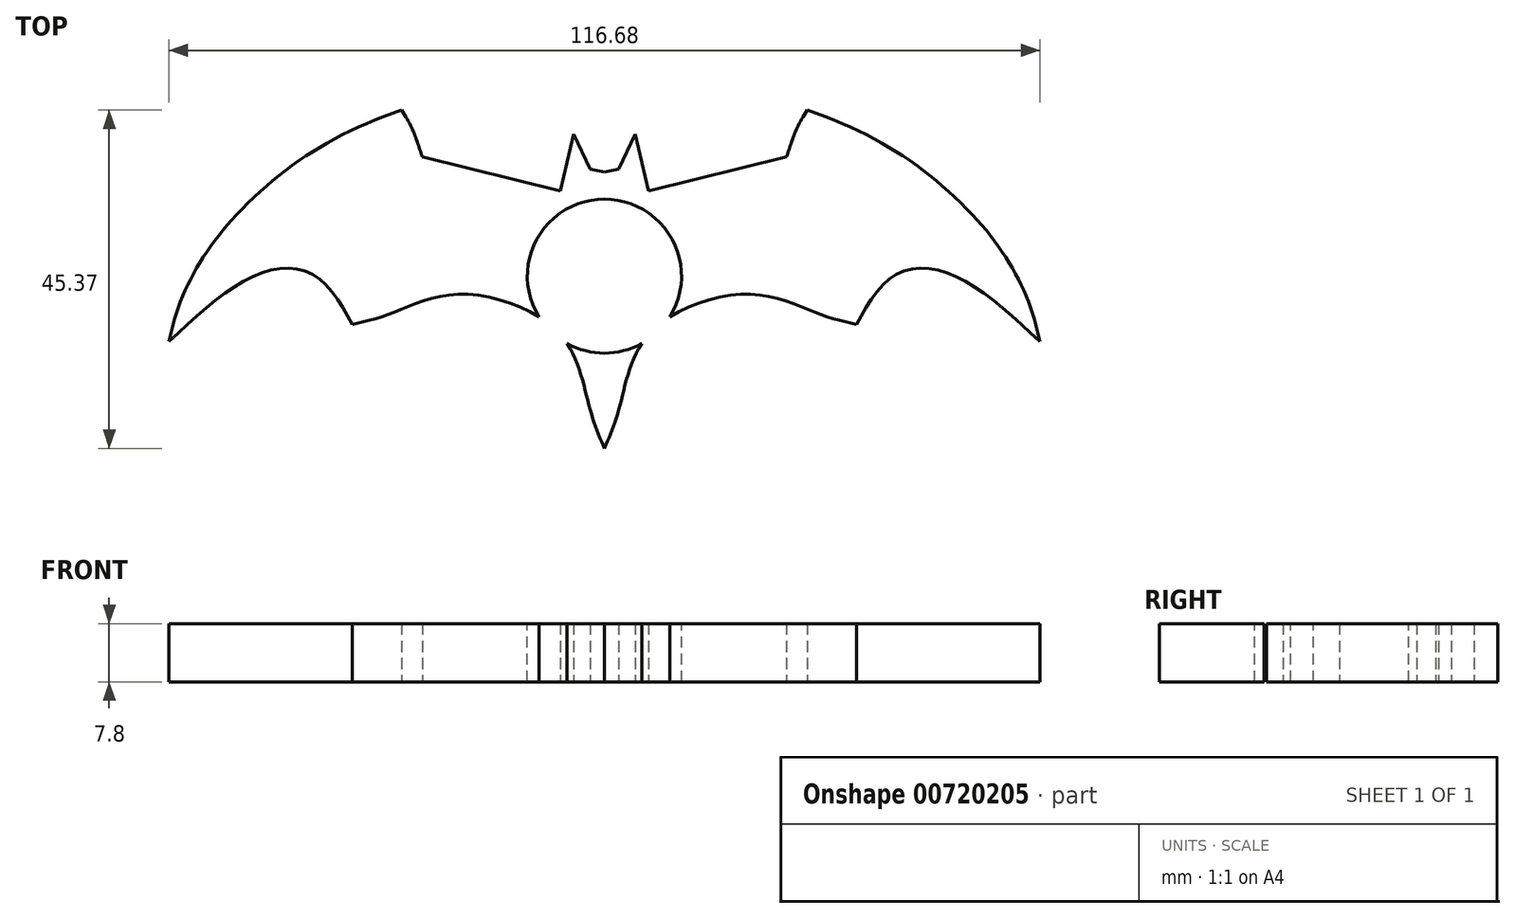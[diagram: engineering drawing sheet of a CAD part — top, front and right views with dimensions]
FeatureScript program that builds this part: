
annotation { "Feature Type Name" : "Feature", "Feature Type Description" : "" }
export const myFeature = defineFeature(function(context is Context, id is Id, definition is map)
    precondition{}
    {
        {
            var Q0;
            Q0=qCreatedBy(makeId("Top.planeOp"),FACE);
            var sketch = newSketch(context, id + "F0", { "sketchPlane" : qUnion([Q0])});
            skFitSpline(sketch, "E0", {"points": [v(28.16, 9) * mm, v(32.71, 14.67) * mm, v(39.1, 14.43) * mm, v(48.61, 7.12) * mm], "startDerivative": vector(11.17, 22.42) * mm, "endDerivative": vector(23.62, -22.06) * mm});
            skFitSpline(sketch, "E1", {"points": [v(48.61, 7.12) * mm, v(41.08, 21.26) * mm], "startDerivative": vector(-2.78, 14.6) * mm, "endDerivative": vector(-12.52, 13.21) * mm});
            skFitSpline(sketch, "E2", {"points": [v(41.08, 21.26) * mm, v(22.65, 32.96) * mm], "startDerivative": vector(-14.9, 15.72) * mm, "endDerivative": vector(-23.64, 8) * mm});
            skFitSpline(sketch, "E3", {"points": [v(22.65, 32.96) * mm, v(20.34, 27.75) * mm], "startDerivative": vector(-4.17, -5.91) * mm, "endDerivative": vector(-1.74, -4.87) * mm});
            skFitSpline(sketch, "E4", {"points": [v(20.34, 27.75) * mm, v(4.92, 23.93) * mm], "startDerivative": vector(-15.41, -3.82) * mm, "endDerivative": vector(-15.41, -3.82) * mm});
            skFitSpline(sketch, "E5", {"points": [v(4.92, 23.93) * mm, v(3.42, 30.3) * mm], "startDerivative": vector(-1.5, 6.37) * mm, "endDerivative": vector(-1.5, 6.37) * mm});
            skFitSpline(sketch, "E6", {"points": [v(3.42, 30.3) * mm, v(1.56, 26.36) * mm], "startDerivative": vector(-1.85, -3.94) * mm, "endDerivative": vector(-1.85, -3.94) * mm});
            skFitSpline(sketch, "E7", {"points": [v(1.56, 26.36) * mm, v(0, 26.05) * mm], "startDerivative": vector(-1.56, -0.3) * mm, "endDerivative": vector(-1.56, -0.3) * mm});
            skFitSpline(sketch, "E8.MirrorCS", {"points": [v(-20.34, 27.75) * mm, v(-4.92, 23.93) * mm], "startDerivative": vector(15.41, -3.82) * mm, "endDerivative": vector(15.41, -3.82) * mm});
            skFitSpline(sketch, "E9.MirrorCS", {"points": [v(-41.08, 21.26) * mm, v(-22.65, 32.96) * mm], "startDerivative": vector(14.9, 15.72) * mm, "endDerivative": vector(23.64, 8) * mm});
            skFitSpline(sketch, "E10.MirrorCS", {"points": [v(-28.16, 9) * mm, v(-32.71, 14.67) * mm, v(-39.1, 14.43) * mm, v(-48.61, 7.12) * mm], "startDerivative": vector(-11.17, 22.42) * mm, "endDerivative": vector(-23.62, -22.06) * mm});
            skFitSpline(sketch, "E11.0", {"points": [v(0, -4.84) * mm, v(1.72, -0.1) * mm, v(5, 7.94) * mm, v(16.3, 12.38) * mm, v(23.87, 10.22) * mm, v(28.16, 9) * mm]});
            skFitSpline(sketch, "E12.MirrorCS", {"points": [v(-48.61, 7.12) * mm, v(-41.08, 21.26) * mm], "startDerivative": vector(2.78, 14.6) * mm, "endDerivative": vector(12.52, 13.21) * mm});
            skFitSpline(sketch, "E13.MirrorCS", {"points": [v(0, -4.84) * mm, v(-1.72, -0.1) * mm, v(-5, 7.94) * mm, v(-16.3, 12.38) * mm, v(-23.87, 10.22) * mm, v(-28.16, 9) * mm]});
            skFitSpline(sketch, "E14.MirrorCS", {"points": [v(-4.92, 23.93) * mm, v(-3.42, 30.3) * mm], "startDerivative": vector(1.5, 6.37) * mm, "endDerivative": vector(1.5, 6.37) * mm});
            skFitSpline(sketch, "E15.MirrorCS", {"points": [v(-3.42, 30.3) * mm, v(-1.56, 26.36) * mm], "startDerivative": vector(1.85, -3.94) * mm, "endDerivative": vector(1.85, -3.94) * mm});
            skFitSpline(sketch, "E16.MirrorCS", {"points": [v(-1.56, 26.36) * mm, v(0, 26.05) * mm], "startDerivative": vector(1.56, -0.3) * mm, "endDerivative": vector(1.56, -0.3) * mm});
            skFitSpline(sketch, "E17.MirrorCS", {"points": [v(-22.65, 32.96) * mm, v(-20.34, 27.75) * mm], "startDerivative": vector(4.17, -5.91) * mm, "endDerivative": vector(1.74, -4.87) * mm});
            skFitSpline(sketch, "E18.MirrorCS", {"points": [v(-3.42, 30.3) * mm, v(-1.56, 26.36) * mm], "startDerivative": vector(1.85, -3.94) * mm, "endDerivative": vector(1.85, -3.94) * mm});
            skSolve(sketch);
        }
        {
            var Q0;
            Q0=makeQuery(id+"F0.imprint","IMPRINT",FACE,{"disambiguationData":[TD([[makeQuery(id+"F0.imprint","IMPRINT",EDGE,{"derivedFrom":sQuery(id+"F0.wireOp",EDGE,"E0")}),1.0]])]});
            extrude(context, id + "F1", {"entities" : qUnion([Q0]), "depth" : 6.5 * mm, "offsetDistance" : 25 * mm});
        }
        {
            var Q0;
            Q0=makeQuery(id+"F1.opExtrude","CAP_FACE",FACE,{"disambiguationData":[OSD([sQuery(id+"F0.wireOp",EDGE,"E0"),sQuery(id+"F0.wireOp",EDGE,"E1"),sQuery(id+"F0.wireOp",EDGE,"E2"),sQuery(id+"F0.wireOp",EDGE,"E3"),sQuery(id+"F0.wireOp",EDGE,"E4"),sQuery(id+"F0.wireOp",EDGE,"E5"),sQuery(id+"F0.wireOp",EDGE,"E6"),sQuery(id+"F0.wireOp",EDGE,"E7"),sQuery(id+"F0.wireOp",EDGE,"E8.MirrorCS"),sQuery(id+"F0.wireOp",EDGE,"E9.MirrorCS"),sQuery(id+"F0.wireOp",EDGE,"E10.MirrorCS"),sQuery(id+"F0.wireOp",EDGE,"E11.0"),sQuery(id+"F0.wireOp",EDGE,"E12.MirrorCS"),sQuery(id+"F0.wireOp",EDGE,"E13.MirrorCS"),sQuery(id+"F0.wireOp",EDGE,"E16.MirrorCS"),sQuery(id+"F0.wireOp",EDGE,"E17.MirrorCS"),sQuery(id+"F0.wireOp",EDGE,"E18.MirrorCS"),sQuery(id+"F0.wireOp",EDGE,"E14.MirrorCS")])],"isStart":false});
            var sketch = newSketch(context, id + "F2", { "sketchPlane" : qUnion([Q0])});
            skCircle(sketch, "E19", {"center": v(-25.83, 20.28) * mm, "radius": 6.01 * mm});
            skCircle(sketch, "E20", {"center": v(0, 14.56) * mm, "radius": 6.33 * mm});
            skCircle(sketch, "E21.MirrorC", {"center": v(25.83, 20.28) * mm, "radius": 6.01 * mm});
            skSolve(sketch);
        }
        {
            var Q0;
            Q0=makeQuery(id+"F1.opExtrude","SWEPT_BODY",BODY,{"disambiguationData":[OSD([sQuery(id+"F0.wireOp",EDGE,"E0"),sQuery(id+"F0.wireOp",EDGE,"E1"),sQuery(id+"F0.wireOp",EDGE,"E2"),sQuery(id+"F0.wireOp",EDGE,"E3"),sQuery(id+"F0.wireOp",EDGE,"E4"),sQuery(id+"F0.wireOp",EDGE,"E5"),sQuery(id+"F0.wireOp",EDGE,"E6"),sQuery(id+"F0.wireOp",EDGE,"E7"),sQuery(id+"F0.wireOp",EDGE,"E8.MirrorCS"),sQuery(id+"F0.wireOp",EDGE,"E9.MirrorCS"),sQuery(id+"F0.wireOp",EDGE,"E10.MirrorCS"),sQuery(id+"F0.wireOp",EDGE,"E11.0"),sQuery(id+"F0.wireOp",EDGE,"E12.MirrorCS"),sQuery(id+"F0.wireOp",EDGE,"E13.MirrorCS"),sQuery(id+"F0.wireOp",EDGE,"E16.MirrorCS"),sQuery(id+"F0.wireOp",EDGE,"E17.MirrorCS"),sQuery(id+"F0.wireOp",EDGE,"E18.MirrorCS"),sQuery(id+"F0.wireOp",EDGE,"E14.MirrorCS")])]});
            var Q1;
            Q1=sQuery(id+"F2.wireOp",VERTEX,"E20.center");
            transform(context, id + "F3", {"entities" : qUnion([Q0]), "transformType" : TransformType.SCALE_UNIFORMLY, "scale" : 1.2, "scalePoint" : qUnion([Q1]), "makeCopy" : false});
        }
        {
            var Q0;
            Q0=makeQuery(id+"F1.opExtrude","CAP_FACE",FACE,{"disambiguationData":[OSD([sQuery(id+"F0.wireOp",EDGE,"E0"),sQuery(id+"F0.wireOp",EDGE,"E1"),sQuery(id+"F0.wireOp",EDGE,"E2"),sQuery(id+"F0.wireOp",EDGE,"E3"),sQuery(id+"F0.wireOp",EDGE,"E4"),sQuery(id+"F0.wireOp",EDGE,"E5"),sQuery(id+"F0.wireOp",EDGE,"E6"),sQuery(id+"F0.wireOp",EDGE,"E7"),sQuery(id+"F0.wireOp",EDGE,"E8.MirrorCS"),sQuery(id+"F0.wireOp",EDGE,"E9.MirrorCS"),sQuery(id+"F0.wireOp",EDGE,"E10.MirrorCS"),sQuery(id+"F0.wireOp",EDGE,"E11.0"),sQuery(id+"F0.wireOp",EDGE,"E12.MirrorCS"),sQuery(id+"F0.wireOp",EDGE,"E13.MirrorCS"),sQuery(id+"F0.wireOp",EDGE,"E16.MirrorCS"),sQuery(id+"F0.wireOp",EDGE,"E17.MirrorCS"),sQuery(id+"F0.wireOp",EDGE,"E18.MirrorCS"),sQuery(id+"F0.wireOp",EDGE,"E14.MirrorCS")])],"isStart":false});
            var sketch = newSketch(context, id + "F4", { "sketchPlane" : qUnion([Q0])});
            skCircle(sketch, "E22", {"center": v(0, 14.38) * mm, "radius": 10.33 * mm});
            skSolve(sketch);
        }
        {
            var Q0;
            Q0=makeQuery(id+"F4.imprint","IMPRINT",FACE,{"disambiguationData":[TD([[makeQuery(id+"F4.imprint","IMPRINT",EDGE,{"derivedFrom":sQuery(id+"F4.wireOp",EDGE,"E22")}),1.0]])]});
            extrude(context, id + "F5", {"entities" : qUnion([Q0]), "operationType" : NewBodyOperationType.REMOVE, "oppositeDirection" : true, "depth" : 25 * mm, "offsetDistance" : 25 * mm});
        }
    });
